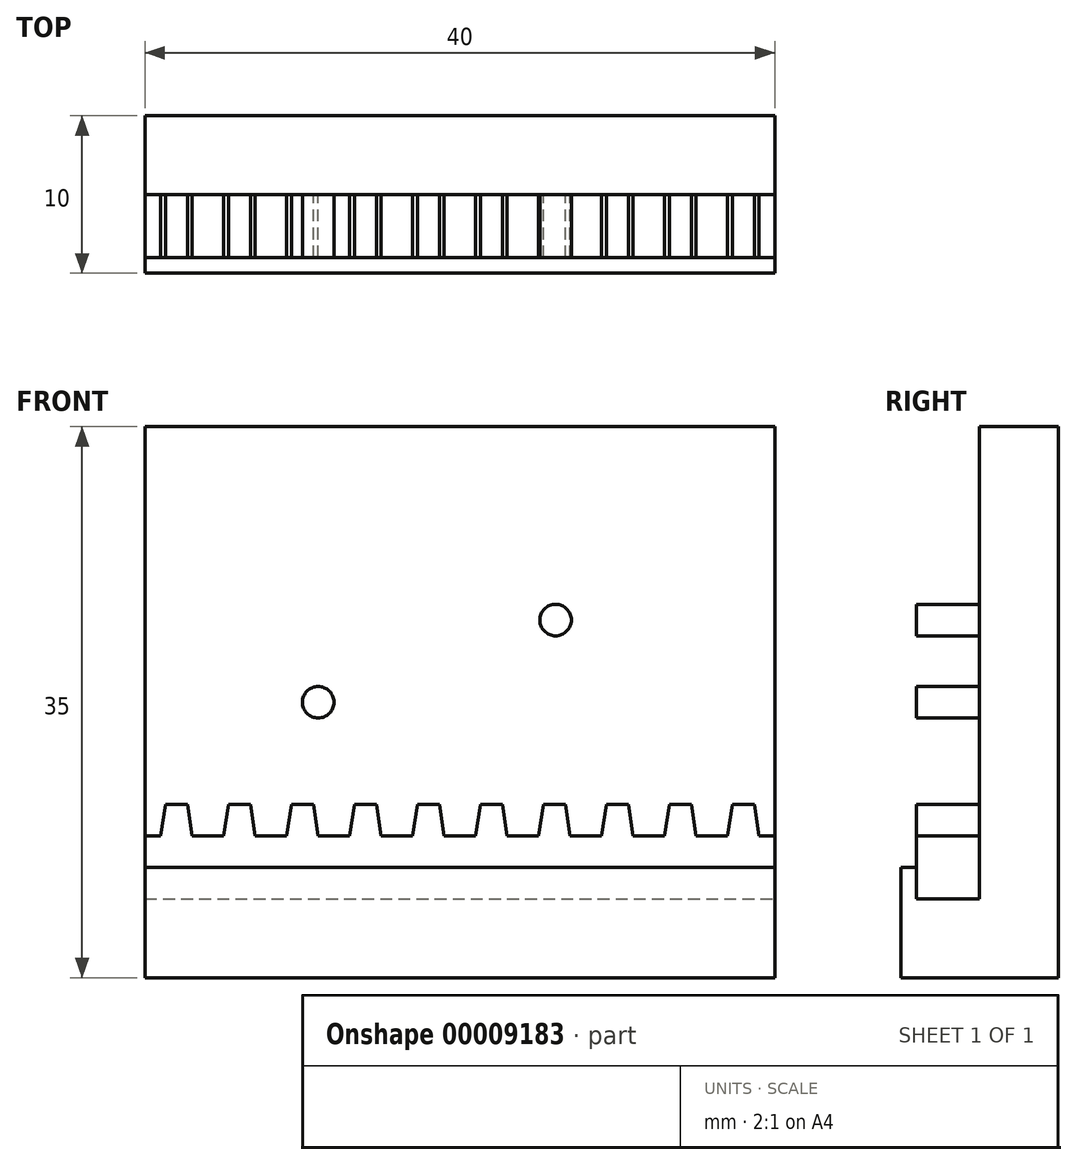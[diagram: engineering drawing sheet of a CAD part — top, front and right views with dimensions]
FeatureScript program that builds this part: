
annotation { "Feature Type Name" : "Feature", "Feature Type Description" : "" }
export const myFeature = defineFeature(function(context is Context, id is Id, definition is map)
    precondition{}
    {
        {
            var Q0;
            Q0=qCreatedBy(makeId("Front.planeOp"),FACE);
            var sketch = newSketch(context, id + "F0", { "sketchPlane" : qUnion([Q0])});
            skLineSegment(sketch, "E0.rect.bottom", {"start": v(-20, 17.5) * mm, "end": v(20, 17.5) * mm});
            skLineSegment(sketch, "E0.rect.top", {"start": v(-20, -17.5) * mm, "end": v(20, -17.5) * mm});
            skLineSegment(sketch, "E0.rect.left", {"start": v(-20, 17.5) * mm, "end": v(-20, -17.5) * mm});
            skLineSegment(sketch, "E0.rect.right", {"start": v(20, 17.5) * mm, "end": v(20, -17.5) * mm});
            skPoint(sketch, "E0.rect.middle", {"position": v(0, 0) * mm});
            skSolve(sketch);
        }
        {
            var Q0;
            Q0 = qSketchRegion(id + "F0", true);
            extrude(context, id + "F1", {"entities" : qUnion([Q0]), "depth" : 10 * mm});
        }
        {
            var Q0;
            Q0=makeQuery(id+"F1.opExtrude","CAP_FACE",FACE,{"disambiguationData":[OSD([sQuery(id+"F0.wireOp",EDGE,"E0.rect.bottom"),sQuery(id+"F0.wireOp",EDGE,"E0.rect.top"),sQuery(id+"F0.wireOp",EDGE,"E0.rect.left"),sQuery(id+"F0.wireOp",EDGE,"E0.rect.right")])],"isStart":false});
            var sketch = newSketch(context, id + "F2", { "sketchPlane" : qUnion([Q0])});
            skLineSegment(sketch, "E1.bottom", {"start": v(-20, 17.5) * mm, "end": v(20, 17.5) * mm});
            skLineSegment(sketch, "E1.top", {"start": v(-20, -12.5) * mm, "end": v(20, -12.5) * mm});
            skLineSegment(sketch, "E1.left", {"start": v(-20, 17.5) * mm, "end": v(-20, -12.5) * mm});
            skLineSegment(sketch, "E1.right", {"start": v(20, 17.5) * mm, "end": v(20, -12.5) * mm});
            skSolve(sketch);
        }
        {
            var Q0;
            Q0 = qSketchRegion(id + "F2", true);
            extrude(context, id + "F3", {"entities" : qUnion([Q0]), "operationType" : NewBodyOperationType.REMOVE, "oppositeDirection" : true, "depth" : 5 * mm});
        }
        {
            var Q0;
            Q0=makeQuery(id+"F1.opExtrude","SWEPT_FACE",FACE,{"disambiguationData":[OSD([sQuery(id+"F0.wireOp",EDGE,"E0.rect.right")])]});
            var sketch = newSketch(context, id + "F4", { "sketchPlane" : qUnion([Q0])});
            skLineSegment(sketch, "E2.bottom", {"start": v(-10, -12.5) * mm, "end": v(-9, -12.5) * mm});
            skLineSegment(sketch, "E2.top", {"start": v(-10, -10.5) * mm, "end": v(-9, -10.5) * mm});
            skLineSegment(sketch, "E2.left", {"start": v(-10, -12.5) * mm, "end": v(-10, -10.5) * mm});
            skLineSegment(sketch, "E2.right", {"start": v(-9, -12.5) * mm, "end": v(-9, -10.5) * mm});
            skSolve(sketch);
        }
        {
            var Q0;
            Q0 = qSketchRegion(id + "F4", true);
            var Q1;
            Q1=makeQuery(id+"F1.opExtrude","SWEPT_FACE",FACE,{"disambiguationData":[OSD([sQuery(id+"F0.wireOp",EDGE,"E0.rect.left")])]});
            extrude(context, id + "F5", {"entities" : qUnion([Q0]), "operationType" : NewBodyOperationType.ADD, "endBound" : BoundingType.UP_TO_SURFACE, "oppositeDirection" : true, "endBoundEntityFace" : qUnion([Q1]), "depth" : 25 * mm});
        }
        {
            var Q0;
            Q0=makeQuery(id+"F3.boolean.opBoolean","COPY",FACE,{"derivedFrom":makeQuery(id+"F3.opExtrude","CAP_FACE",FACE,{"disambiguationData":[OSD([sQuery(id+"F2.wireOp",EDGE,"E1.bottom"),sQuery(id+"F2.wireOp",EDGE,"E1.top"),sQuery(id+"F2.wireOp",EDGE,"E1.left"),sQuery(id+"F2.wireOp",EDGE,"E1.right")])],"isStart":false})});
            var sketch = newSketch(context, id + "F6", { "sketchPlane" : qUnion([Q0])});
            skCircle(sketch, "E3", {"center": v(-9, 0) * mm, "radius": 1 * mm});
            skCircle(sketch, "E4", {"center": v(6.08, 5.22) * mm, "radius": 1 * mm});
            skSolve(sketch);
        }
        {
            var Q0;
            Q0 = qSketchRegion(id + "F6", true);
            var Q1;
            Q1 = qSketchRegion(id + "F8", true);
            extrude(context, id + "F7", {"entities" : qUnion([Q0, Q1]), "operationType" : NewBodyOperationType.ADD, "depth" : 4 * mm});
        }
        {
            var Q0;
            Q0=makeQuery(id+"F3.boolean.opBoolean","COPY",FACE,{"derivedFrom":makeQuery(id+"F3.opExtrude","CAP_FACE",FACE,{"disambiguationData":[OSD([sQuery(id+"F2.wireOp",EDGE,"E1.bottom"),sQuery(id+"F2.wireOp",EDGE,"E1.top"),sQuery(id+"F2.wireOp",EDGE,"E1.left"),sQuery(id+"F2.wireOp",EDGE,"E1.right")])],"isStart":false})});
            var sketch = newSketch(context, id + "F8", { "sketchPlane" : qUnion([Q0])});
            skLineSegment(sketch, "E5.bottom", {"start": v(20, -8.5) * mm, "end": v(-20, -8.5) * mm});
            skLineSegment(sketch, "E5.top", {"start": v(20, -12.5) * mm, "end": v(-20, -12.5) * mm});
            skLineSegment(sketch, "E5.left", {"start": v(20, -8.5) * mm, "end": v(20, -12.5) * mm});
            skLineSegment(sketch, "E5.right", {"start": v(-20, -8.5) * mm, "end": v(-20, -12.5) * mm});
            skLineSegment(sketch, "E6", {"start": v(-18, -8.5) * mm, "end": v(-18, -12.5) * mm, "construction": true});
            skLineSegment(sketch, "E7", {"start": v(-19, -8.5) * mm, "end": v(-18.7, -6.5) * mm});
            skLineSegment(sketch, "E8", {"start": v(-18.7, -6.5) * mm, "end": v(-18, -6.5) * mm});
            skLineSegment(sketch, "E9.0.MirrorCS", {"start": v(-17, -8.5) * mm, "end": v(-17.3, -6.5) * mm});
            skLineSegment(sketch, "E10.0.MirrorCS", {"start": v(-17.3, -6.5) * mm, "end": v(-18, -6.5) * mm});
            skLineSegment(sketch, "E11.1.0.0", {"start": v(-15, -8.5) * mm, "end": v(-14.7, -6.5) * mm});
            skLineSegment(sketch, "E11.1.0.1", {"start": v(-14.7, -6.5) * mm, "end": v(-14, -6.5) * mm});
            skLineSegment(sketch, "E11.1.0.2", {"start": v(-13.3, -6.5) * mm, "end": v(-14, -6.5) * mm});
            skLineSegment(sketch, "E11.1.0.3", {"start": v(-13, -8.5) * mm, "end": v(-13.3, -6.5) * mm});
            skLineSegment(sketch, "E11.2.0.0", {"start": v(-11, -8.5) * mm, "end": v(-10.7, -6.5) * mm});
            skLineSegment(sketch, "E11.2.0.1", {"start": v(-10.7, -6.5) * mm, "end": v(-10, -6.5) * mm});
            skLineSegment(sketch, "E11.2.0.2", {"start": v(-9.3, -6.5) * mm, "end": v(-10, -6.5) * mm});
            skLineSegment(sketch, "E11.2.0.3", {"start": v(-9, -8.5) * mm, "end": v(-9.3, -6.5) * mm});
            skLineSegment(sketch, "E11.3.0.0", {"start": v(-7, -8.5) * mm, "end": v(-6.7, -6.5) * mm});
            skLineSegment(sketch, "E11.3.0.1", {"start": v(-6.7, -6.5) * mm, "end": v(-6, -6.5) * mm});
            skLineSegment(sketch, "E11.3.0.2", {"start": v(-5.3, -6.5) * mm, "end": v(-6, -6.5) * mm});
            skLineSegment(sketch, "E11.3.0.3", {"start": v(-5, -8.5) * mm, "end": v(-5.3, -6.5) * mm});
            skLineSegment(sketch, "E11.4.0.0", {"start": v(-3, -8.5) * mm, "end": v(-2.7, -6.5) * mm});
            skLineSegment(sketch, "E11.4.0.1", {"start": v(-2.7, -6.5) * mm, "end": v(-2, -6.5) * mm});
            skLineSegment(sketch, "E11.4.0.2", {"start": v(-1.3, -6.5) * mm, "end": v(-2, -6.5) * mm});
            skLineSegment(sketch, "E11.4.0.3", {"start": v(-1, -8.5) * mm, "end": v(-1.3, -6.5) * mm});
            skLineSegment(sketch, "E11.5.0.0", {"start": v(1, -8.5) * mm, "end": v(1.3, -6.5) * mm});
            skLineSegment(sketch, "E11.5.0.1", {"start": v(1.3, -6.5) * mm, "end": v(2, -6.5) * mm});
            skLineSegment(sketch, "E11.5.0.2", {"start": v(2.7, -6.5) * mm, "end": v(2, -6.5) * mm});
            skLineSegment(sketch, "E11.5.0.3", {"start": v(3, -8.5) * mm, "end": v(2.7, -6.5) * mm});
            skLineSegment(sketch, "E11.6.0.0", {"start": v(5, -8.5) * mm, "end": v(5.3, -6.5) * mm});
            skLineSegment(sketch, "E11.6.0.1", {"start": v(5.3, -6.5) * mm, "end": v(6, -6.5) * mm});
            skLineSegment(sketch, "E11.6.0.2", {"start": v(6.7, -6.5) * mm, "end": v(6, -6.5) * mm});
            skLineSegment(sketch, "E11.6.0.3", {"start": v(7, -8.5) * mm, "end": v(6.7, -6.5) * mm});
            skLineSegment(sketch, "E11.7.0.0", {"start": v(9, -8.5) * mm, "end": v(9.3, -6.5) * mm});
            skLineSegment(sketch, "E11.7.0.1", {"start": v(9.3, -6.5) * mm, "end": v(10, -6.5) * mm});
            skLineSegment(sketch, "E11.7.0.2", {"start": v(10.7, -6.5) * mm, "end": v(10, -6.5) * mm});
            skLineSegment(sketch, "E11.7.0.3", {"start": v(11, -8.5) * mm, "end": v(10.7, -6.5) * mm});
            skLineSegment(sketch, "E11.8.0.0", {"start": v(13, -8.5) * mm, "end": v(13.3, -6.5) * mm});
            skLineSegment(sketch, "E11.8.0.1", {"start": v(13.3, -6.5) * mm, "end": v(14, -6.5) * mm});
            skLineSegment(sketch, "E11.8.0.2", {"start": v(14.7, -6.5) * mm, "end": v(14, -6.5) * mm});
            skLineSegment(sketch, "E11.8.0.3", {"start": v(15, -8.5) * mm, "end": v(14.7, -6.5) * mm});
            skLineSegment(sketch, "E11.9.0.0", {"start": v(17, -8.5) * mm, "end": v(17.3, -6.5) * mm});
            skLineSegment(sketch, "E11.9.0.1", {"start": v(17.3, -6.5) * mm, "end": v(18, -6.5) * mm});
            skLineSegment(sketch, "E11.9.0.2", {"start": v(18.7, -6.5) * mm, "end": v(18, -6.5) * mm});
            skLineSegment(sketch, "E11.9.0.3", {"start": v(19, -8.5) * mm, "end": v(18.7, -6.5) * mm});
            skLineSegment(sketch, "E11.direction1", {"start": v(-19, -8.5) * mm, "end": v(-15, -8.5) * mm, "construction": true});
            skSolve(sketch);
        }
        {
            var Q0;
            Q0 = qSketchRegion(id + "F8", true);
            extrude(context, id + "F9", {"entities" : qUnion([Q0]), "depth" : 4 * mm});
        }
    });
